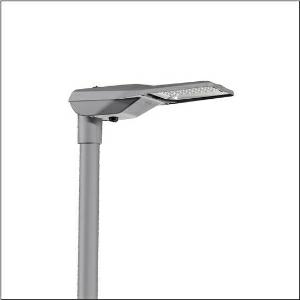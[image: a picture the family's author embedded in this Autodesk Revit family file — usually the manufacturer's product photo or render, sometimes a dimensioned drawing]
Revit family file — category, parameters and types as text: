
# Revit family: streetlight_sl_21_mini___st0_5a_5xe2b33t08jb_d15d
name_source: partatom
category: Lighting Fixtures
units: mm (PartAtom-declared; Revit-internal decimal feet)

## family parameters
Cut with Voids When Loaded = No
Host = Face
Light Source = No
Part Type = Normal
Room Calculation Point = No
Round Connector Dimension = Use Diameter
Shared = No

## types (1)
- --- (1 x LED, 12940 lm, 88.6 W, 3000K)
    Apparent Load = 89 VA
    CIE Flux Codes = 43 76 97 100 100
    Color Rendering = 70
    Color Temperature = 3000K
    Default Elevation = 1800 mm
    Description = Streetlight SL 21 mini, mast luminaire, primary light control with lens, of PMMA, primary optical cover: cover, of toughened safety glass, transparent, light distribution: ST0.5a, light emission: direct distribution, primary light characteristic: asymmetric, installation type: side-entry, post-top, LED, High Power LED, rated luminous flux: 12.940lm, luminous efficacy: 146lm/W, light colour: 730, colour temperature: 3000K, control gear: D4i, control: overheat protection, constant luminous flux control, time-dependent luminous flux control, flexible luminous flux parameterisation, pre-setting: logarithmic dimming characteristic, mains connection: 220..240V, AC, 50/60Hz, start of lifetime: 89W, end of service life: 92W, reduction: 41W, luminaire housing, of diecast aluminium, powder-coated, SITECO metallic grey (DB 702S), corrosivity category C5 high according to DIN EN ISO 12944, please order mast flange separately, inclination adjustable: 0°, 5°, 10°, 15°, sealing non-destructively replaceable, multi-level sealing system, length: 628mm, width: 235mm, height: 110mm, mast flange for spigot size: 42mm (side-entry): 5XC10008XM4, 60/48mm (side-entry/post-top): 5XC10108XM2, 76/60mm (side-entry/post-top): 5XC10108XM1, mounting height: 4..8m, Smart Interface below and above, protection rating (complete): IP66, insulation class (complete): insulation class II (safety insulation), certification: CE, ENEC, ENEC+, VDE, impact resistance: IK10, permissible operating ambient temperature for outdoor applications: -40..+50°C, standard-compliant lighting for roads and squares, packaging unit: 1 piece

Light Distribution: ST0.5a
    Height = 110 mm
    Lamp = 1 x LED
    Lamp Light Flux = 12940 lm
    Lamp Power = 88.6 W
    Lamp count = 1
    Length = 625 mm
    Luminous efficacy = 146 lm/W
    Manufacturer = Siteco
    ModVariant = No
    Model = 5XE2B33T08JB
    Number of Poles = 1
    OnlyDefault = Yes
    Power Factor = 1
    Product Name = Streetlight SL 21 mini | ST0.5a
    Product group = mast luminaire | pylon top
    ProductGroupID = 6100
    Protection Class = Protection class II
    Protection Degree = IP 66
    RLX_Detail_Level = 1
    RLX_Emergency_Light_Flux = 0 lm
    RLX_Emergency_Type = 0
    RLX_Emergency_Type_DB = No
    RlxData = <blob elided: 37617 chars, md5=f5d50b67>
    Socket = socket
    Standby Power = 0 W
    System Light Flux = 12940 lm
    System Power = 89 W
    Type Comments = factory setting: luminous flux: 100 % | dim-lin: 254 | 915 mA
    Type Image = l_1003514.jpg
    URL = http://relux.com
    VarID = @adj_031919
    Voltage = 0 V
    Weight = 0.00 kg
    Width = 234 mm

## geometry (parser evidence)
native form markers: Blend x4, Sweep x10
no freeform markers — native parametric forms only
